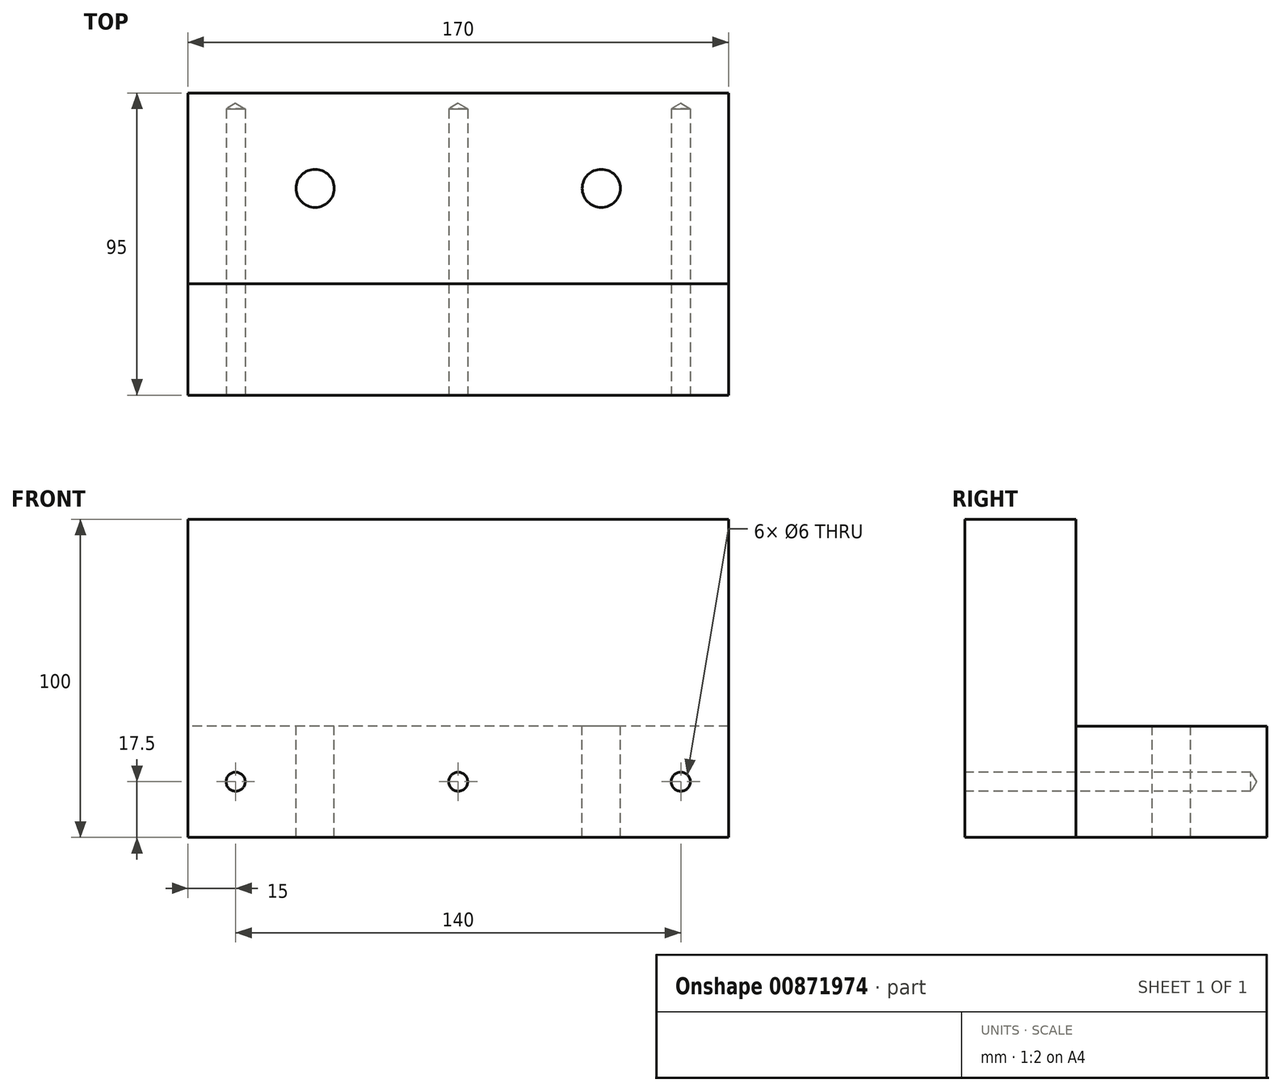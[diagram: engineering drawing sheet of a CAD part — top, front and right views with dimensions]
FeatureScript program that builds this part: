
annotation { "Feature Type Name" : "Feature", "Feature Type Description" : "" }
export const myFeature = defineFeature(function(context is Context, id is Id, definition is map)
    precondition{}
    {
        {
            var Q0;
            Q0=qCreatedBy(makeId("Top.planeOp"),FACE);
            var sketch = newSketch(context, id + "F0", { "sketchPlane" : qUnion([Q0])});
            skLineSegment(sketch, "E0.bottom", {"start": v(85, -30) * mm, "end": v(-85, -30) * mm});
            skLineSegment(sketch, "E0.top", {"start": v(85, 30) * mm, "end": v(-85, 30) * mm});
            skLineSegment(sketch, "E0.left", {"start": v(85, -30) * mm, "end": v(85, 30) * mm});
            skLineSegment(sketch, "E0.right", {"start": v(-85, -30) * mm, "end": v(-85, 30) * mm});
            skPoint(sketch, "E0.middle", {"position": v(0, 0) * mm});
            skSolve(sketch);
        }
        {
            var Q0;
            Q0 = qSketchRegion(id + "F0", true);
            extrude(context, id + "F1", {"entities" : qUnion([Q0]), "depth" : 35 * mm, "offsetDistance" : 25 * mm});
        }
        {
            var Q0;
            Q0=makeQuery(id+"F1.opExtrude","SWEPT_FACE",FACE,{"disambiguationData":[OSD([sQuery(id+"F0.wireOp",EDGE,"E0.bottom")])]});
            var sketch = newSketch(context, id + "F2", { "sketchPlane" : qUnion([Q0])});
            skLineSegment(sketch, "E1.bottom", {"start": v(-85, 0) * mm, "end": v(85, 0) * mm});
            skLineSegment(sketch, "E1.top", {"start": v(-85, 100) * mm, "end": v(85, 100) * mm});
            skLineSegment(sketch, "E1.left", {"start": v(-85, 0) * mm, "end": v(-85, 100) * mm});
            skLineSegment(sketch, "E1.right", {"start": v(85, 0) * mm, "end": v(85, 100) * mm});
            skSolve(sketch);
        }
        {
            var Q0;
            Q0 = qSketchRegion(id + "F2", true);
            extrude(context, id + "F3", {"entities" : qUnion([Q0]), "depth" : 35 * mm, "offsetDistance" : 25 * mm});
        }
        {
            var Q0;
            Q0=makeQuery(id+"F1.opExtrude","CAP_FACE",FACE,{"disambiguationData":[OSD([sQuery(id+"F0.wireOp",EDGE,"E0.bottom"),sQuery(id+"F0.wireOp",EDGE,"E0.top"),sQuery(id+"F0.wireOp",EDGE,"E0.left"),sQuery(id+"F0.wireOp",EDGE,"E0.right")])],"isStart":false});
            var sketch = newSketch(context, id + "F4", { "sketchPlane" : qUnion([Q0])});
            skCircle(sketch, "E2", {"center": v(45, 0) * mm, "radius": 6 * mm});
            skCircle(sketch, "E3", {"center": v(-45, 0) * mm, "radius": 6 * mm});
            skLineSegment(sketch, "E4", {"start": v(-45, 0) * mm, "end": v(45, 0) * mm, "construction": true});
            skSolve(sketch);
        }
        {
            var Q0;
            Q0 = qSketchRegion(id + "F4", true);
            extrude(context, id + "F5", {"entities" : qUnion([Q0]), "operationType" : NewBodyOperationType.REMOVE, "endBound" : BoundingType.THROUGH_ALL, "oppositeDirection" : true, "depth" : 25 * mm, "offsetDistance" : 25 * mm});
        }
        {
            var Q0;
            Q0=makeQuery(id+"F3.opExtrude","CAP_FACE",FACE,{"disambiguationData":[OSD([sQuery(id+"F2.wireOp",EDGE,"E1.bottom"),sQuery(id+"F2.wireOp",EDGE,"E1.top"),sQuery(id+"F2.wireOp",EDGE,"E1.left"),sQuery(id+"F2.wireOp",EDGE,"E1.right")])],"isStart":false});
            var sketch = newSketch(context, id + "F6", { "sketchPlane" : qUnion([Q0])});
            skLineSegment(sketch, "E5", {"start": v(-70, 17.5) * mm, "end": v(0, 17.5) * mm});
            skLineSegment(sketch, "E6", {"start": v(0, 17.5) * mm, "end": v(70, 17.5) * mm});
            skSolve(sketch);
        }
        {
            var Q0;
            Q0=sQuery(id+"F6.wireOp",VERTEX,"E5.start");
            var Q1;
            Q1=sQuery(id+"F6.wireOp",VERTEX,"E5.end");
            var Q2;
            Q2=sQuery(id+"F6.wireOp",VERTEX,"E6.end");
            var Q3;
            Q3=makeQuery(id+"F1.opExtrude","SWEPT_BODY",BODY,{"disambiguationData":[OSD([sQuery(id+"F0.wireOp",EDGE,"E0.bottom"),sQuery(id+"F0.wireOp",EDGE,"E0.top"),sQuery(id+"F0.wireOp",EDGE,"E0.left"),sQuery(id+"F0.wireOp",EDGE,"E0.right")])]});
            var Q4;
            Q4=makeQuery(id+"F3.opExtrude","SWEPT_BODY",BODY,{"disambiguationData":[OSD([sQuery(id+"F2.wireOp",EDGE,"E1.bottom"),sQuery(id+"F2.wireOp",EDGE,"E1.top"),sQuery(id+"F2.wireOp",EDGE,"E1.left"),sQuery(id+"F2.wireOp",EDGE,"E1.right")])]});
            hole(context, id + "F7", {"style" : HoleStyle.SIMPLE, "endStyle" : HoleEndStyle.BLIND, "holeDiameter" : 6 * mm, "majorDiameter" : 5 * mm, "holeDepth" : 90 * mm, "isTappedThrough" : true, "tappedDepth" : 12 * mm, "tapClearance" : 3, "locations" : qUnion([Q0, Q1, Q2]), "scope" : qUnion([Q3, Q4])});
        }
    });
